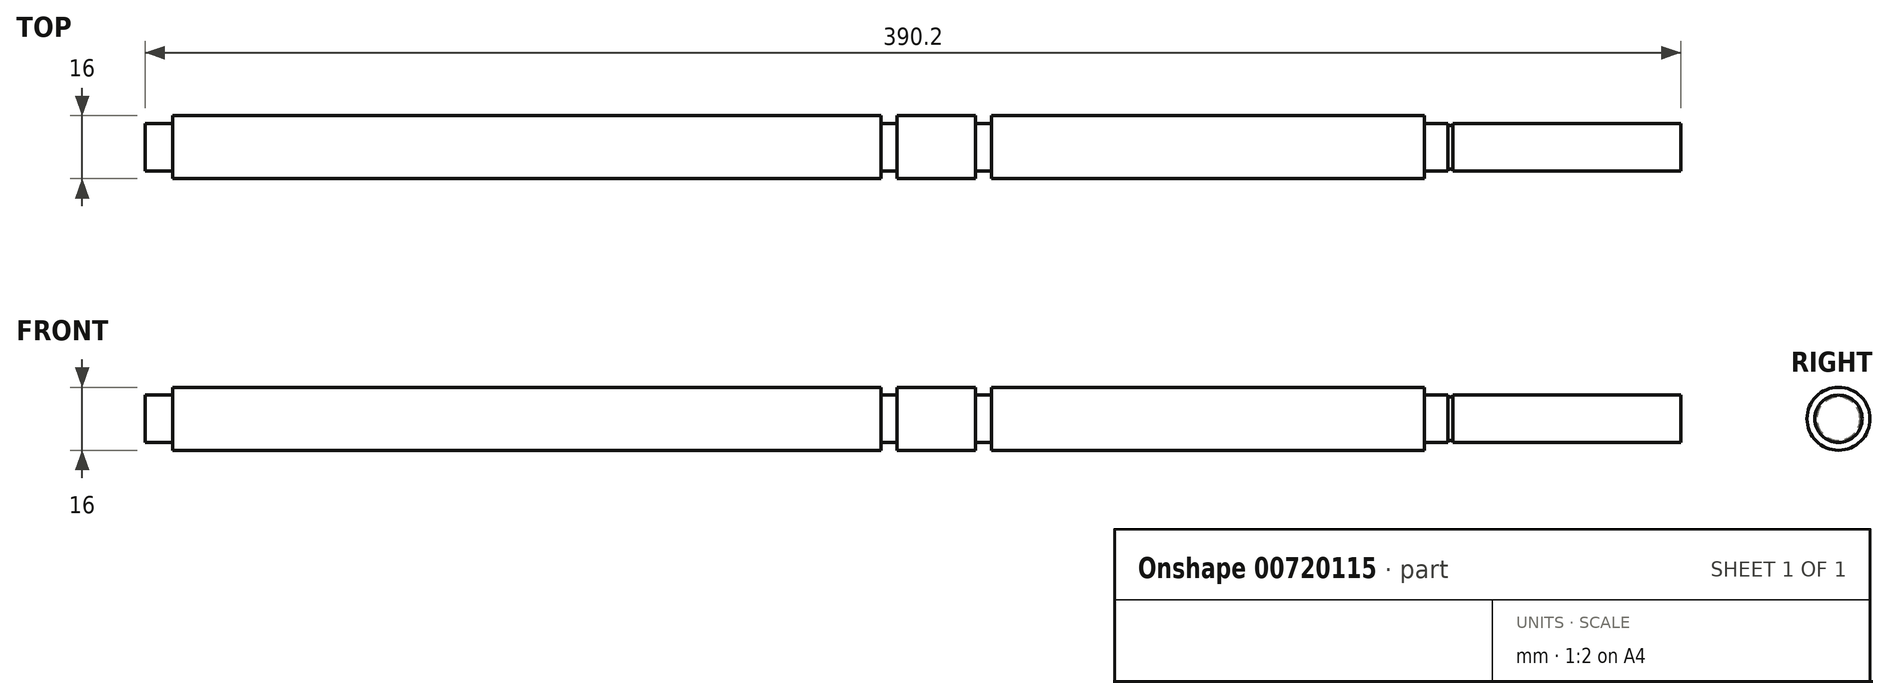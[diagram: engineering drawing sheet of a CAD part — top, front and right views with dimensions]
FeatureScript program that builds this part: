
annotation { "Feature Type Name" : "Feature", "Feature Type Description" : "" }
export const myFeature = defineFeature(function(context is Context, id is Id, definition is map)
    precondition{}
    {
        {
            var Q0;
            Q0=qCreatedBy(makeId("Front.planeOp"),FACE);
            var sketch = newSketch(context, id + "F0", { "sketchPlane" : qUnion([Q0])});
            skLineSegment(sketch, "E0", {"start": v(0, 0) * mm, "end": v(0, 6) * mm});
            skLineSegment(sketch, "E1", {"start": v(0, 6) * mm, "end": v(7, 6) * mm});
            skLineSegment(sketch, "E2", {"start": v(7, 6) * mm, "end": v(7, 8) * mm});
            skLineSegment(sketch, "E3", {"start": v(7, 8) * mm, "end": v(187, 8) * mm});
            skLineSegment(sketch, "E4", {"start": v(187, 8) * mm, "end": v(187, 6) * mm});
            skLineSegment(sketch, "E5", {"start": v(187, 6) * mm, "end": v(191, 6) * mm});
            skLineSegment(sketch, "E6", {"start": v(191, 6) * mm, "end": v(191, 8) * mm});
            skLineSegment(sketch, "E7", {"start": v(191, 8) * mm, "end": v(211, 8) * mm});
            skLineSegment(sketch, "E8", {"start": v(211, 8) * mm, "end": v(211, 6) * mm});
            skLineSegment(sketch, "E9", {"start": v(211, 6) * mm, "end": v(215, 6) * mm});
            skLineSegment(sketch, "E10", {"start": v(215, 6) * mm, "end": v(215, 8) * mm});
            skLineSegment(sketch, "E11", {"start": v(215, 8) * mm, "end": v(325, 8) * mm});
            skLineSegment(sketch, "E12", {"start": v(325, 8) * mm, "end": v(325, 6) * mm});
            skLineSegment(sketch, "E13", {"start": v(325, 6) * mm, "end": v(331, 6) * mm});
            skLineSegment(sketch, "E14", {"start": v(331, 6) * mm, "end": v(331, 5.5) * mm});
            skLineSegment(sketch, "E15", {"start": v(331, 5.5) * mm, "end": v(332.2, 5.5) * mm});
            skLineSegment(sketch, "E16", {"start": v(332.2, 5.5) * mm, "end": v(332.2, 6) * mm});
            skLineSegment(sketch, "E17", {"start": v(332.2, 6) * mm, "end": v(390.2, 6) * mm});
            skLineSegment(sketch, "E18", {"start": v(390.2, 6) * mm, "end": v(390.2, 0) * mm});
            skLineSegment(sketch, "E19", {"start": v(390.2, 0) * mm, "end": v(0, 0) * mm});
            skSolve(sketch);
        }
        {
            var Q0;
            Q0=makeQuery(id+"F0.imprint","IMPRINT",FACE,{"disambiguationData":[TD([[makeQuery(id+"F0.imprint","IMPRINT",EDGE,{"derivedFrom":sQuery(id+"F0.wireOp",EDGE,"E0")}),-1.0]])]});
            var Q1;
            Q1=sQuery(id+"F0.wireOp",EDGE,"E19");
            revolve(context, id + "F1", {"surfaceOperationType" : NewSurfaceOperationType.NEW, "entities" : qUnion([Q0]), "axis" : qUnion([Q1]), "revolveType" : RevolveType.FULL});
        }
    });
